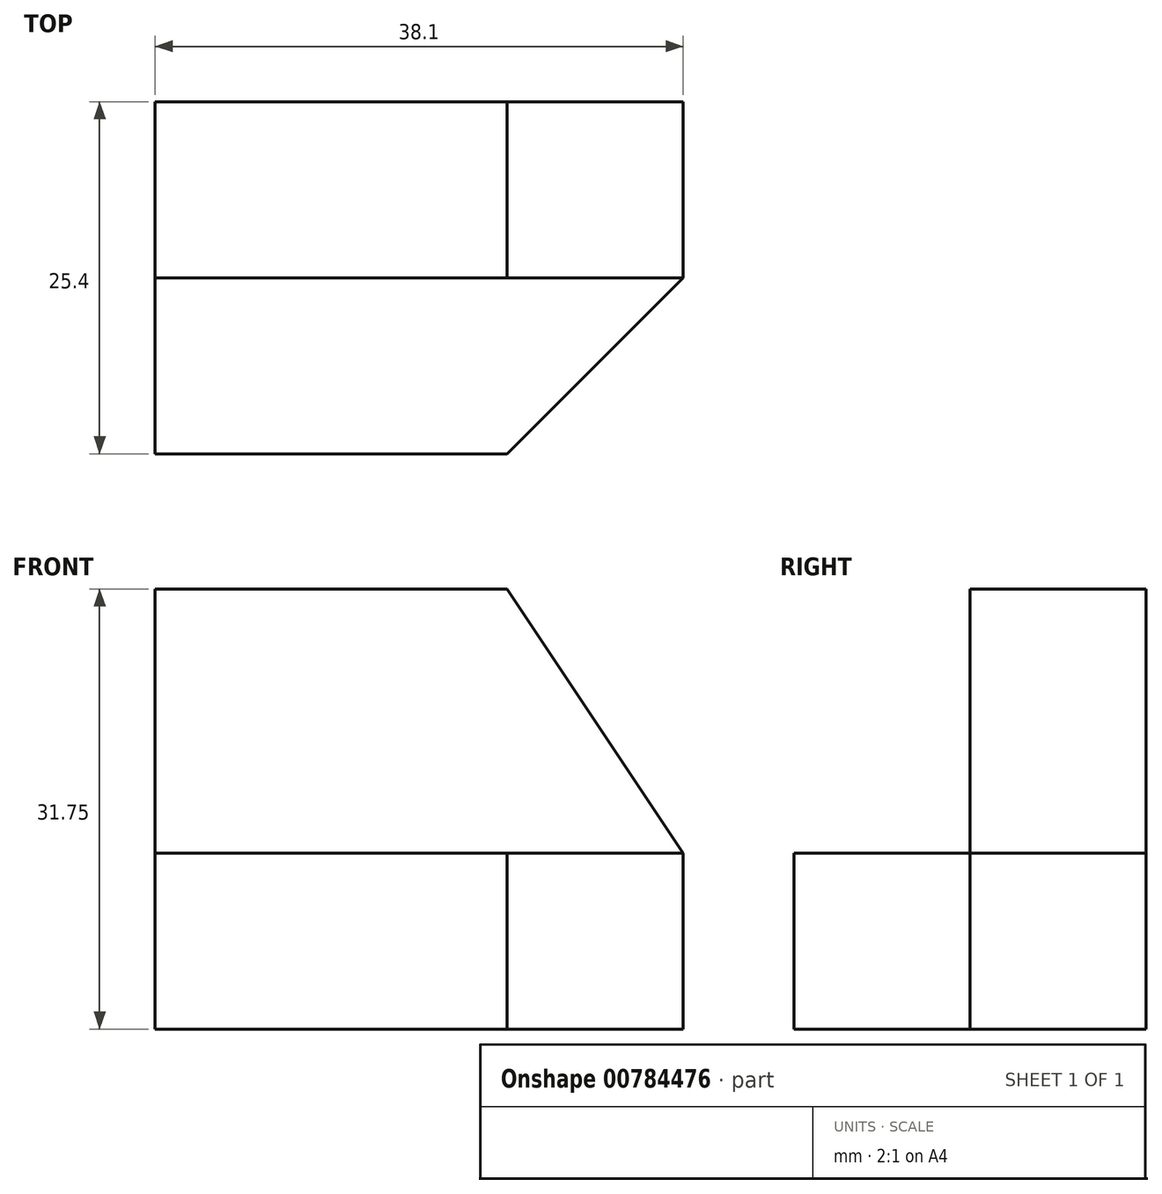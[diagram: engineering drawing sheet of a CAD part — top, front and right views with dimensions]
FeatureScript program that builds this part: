
annotation { "Feature Type Name" : "Feature", "Feature Type Description" : "" }
export const myFeature = defineFeature(function(context is Context, id is Id, definition is map)
    precondition{}
    {
        {
            var Q0;
            Q0=qCreatedBy(makeId("Front.planeOp"),FACE);
            var sketch = newSketch(context, id + "F0", { "sketchPlane" : qUnion([Q0])});
            skLineSegment(sketch, "E0", {"start": v(0, 0) * mm, "end": v(0, 31.75) * mm});
            skLineSegment(sketch, "E1", {"start": v(0, 31.75) * mm, "end": v(38.1, 31.75) * mm});
            skLineSegment(sketch, "E2", {"start": v(38.1, 31.75) * mm, "end": v(38.1, 0) * mm});
            skLineSegment(sketch, "E3", {"start": v(38.1, 0) * mm, "end": v(0, 0) * mm});
            skSolve(sketch);
        }
        {
            var Q0;
            Q0 = qSketchRegion(id + "F0", true);
            extrude(context, id + "F1", {"entities" : qUnion([Q0]), "depth" : 25.4 * mm, "offsetDistance" : 25.4 * mm});
        }
        {
            var Q0;
            Q0=makeQuery(id+"F1.opExtrude","SWEPT_FACE",FACE,{"disambiguationData":[OSD([sQuery(id+"F0.wireOp",EDGE,"E2")])]});
            var sketch = newSketch(context, id + "F2", { "sketchPlane" : qUnion([Q0])});
            skLineSegment(sketch, "E4", {"start": v(0, 0) * mm, "end": v(0, 31.75) * mm});
            skLineSegment(sketch, "E5", {"start": v(0, 31.75) * mm, "end": v(-12.7, 31.75) * mm});
            skLineSegment(sketch, "E6", {"start": v(-12.7, 31.75) * mm, "end": v(-12.7, 12.7) * mm});
            skLineSegment(sketch, "E7", {"start": v(-12.7, 12.7) * mm, "end": v(-25.4, 12.7) * mm});
            skPoint(sketch, "E7.endSnap0", {"position": v(-25.4, 15.88) * mm});
            skLineSegment(sketch, "E8", {"start": v(-25.4, 12.7) * mm, "end": v(-25.4, 0) * mm});
            skLineSegment(sketch, "E9", {"start": v(-25.4, 0) * mm, "end": v(0, 0) * mm});
            skSolve(sketch);
        }
        {
            var Q0;
            {var subQ0=sQuery(id+"F2.wireOp",EDGE,"E6");Q0=makeQuery(id+"F2.imprint","IMPRINT",FACE,{"disambiguationData":[TD([[makeQuery(id+"F2.imprint","IMPRINT",EDGE,{"derivedFrom":subQ0}),-1.0]])]});}
            extrude(context, id + "F3", {"entities" : qUnion([Q0]), "operationType" : NewBodyOperationType.REMOVE, "oppositeDirection" : true, "depth" : 38.1 * mm, "offsetDistance" : 25.4 * mm});
        }
        {
            var Q0;
            Q0=makeQuery(id+"F3.boolean.opBoolean","COPY",FACE,{"derivedFrom":makeQuery(id+"F3.opExtrude","SWEPT_FACE",FACE,{"disambiguationData":[OSD([sQuery(id+"F2.wireOp",EDGE,"E6")])]})});
            var sketch = newSketch(context, id + "F4", { "sketchPlane" : qUnion([Q0])});
            skLineSegment(sketch, "E10", {"start": v(38.1, 31.75) * mm, "end": v(25.4, 31.75) * mm});
            skLineSegment(sketch, "E11", {"start": v(25.4, 31.75) * mm, "end": v(38.1, 12.7) * mm});
            skSolve(sketch);
        }
        {
            var Q0;
            Q0=makeQuery(id+"F4.imprint","IMPRINT",FACE,{"disambiguationData":[TD([[makeQuery(id+"F4.imprint","IMPRINT",EDGE,{"derivedFrom":sQuery(id+"F4.wireOp",EDGE,"E10")}),-1.0]])]});
            extrude(context, id + "F5", {"entities" : qUnion([Q0]), "operationType" : NewBodyOperationType.REMOVE, "oppositeDirection" : true, "depth" : 12.7 * mm, "offsetDistance" : 25.4 * mm});
        }
        {
            var Q0;
            Q0=makeQuery(id+"F3.boolean.opBoolean","COPY",FACE,{"derivedFrom":makeQuery(id+"F3.opExtrude","SWEPT_FACE",FACE,{"disambiguationData":[OSD([sQuery(id+"F2.wireOp",EDGE,"E7")])]})});
            var sketch = newSketch(context, id + "F6", { "sketchPlane" : qUnion([Q0])});
            skLineSegment(sketch, "E12", {"start": v(38.1, -12.7) * mm, "end": v(38.1, -25.4) * mm});
            skLineSegment(sketch, "E13", {"start": v(38.1, -25.4) * mm, "end": v(25.4, -25.4) * mm});
            skLineSegment(sketch, "E14", {"start": v(25.4, -25.4) * mm, "end": v(38.1, -12.7) * mm});
            skSolve(sketch);
        }
        {
            var Q0;
            Q0=makeQuery(id+"F6.imprint","IMPRINT",FACE,{"disambiguationData":[TD([[makeQuery(id+"F6.imprint","IMPRINT",EDGE,{"derivedFrom":sQuery(id+"F6.wireOp",EDGE,"E12")}),-1.0]])]});
            extrude(context, id + "F7", {"entities" : qUnion([Q0]), "operationType" : NewBodyOperationType.REMOVE, "endBound" : BoundingType.UP_TO_NEXT, "oppositeDirection" : true, "depth" : 25.4 * mm, "offsetDistance" : 25.4 * mm});
        }
    });
